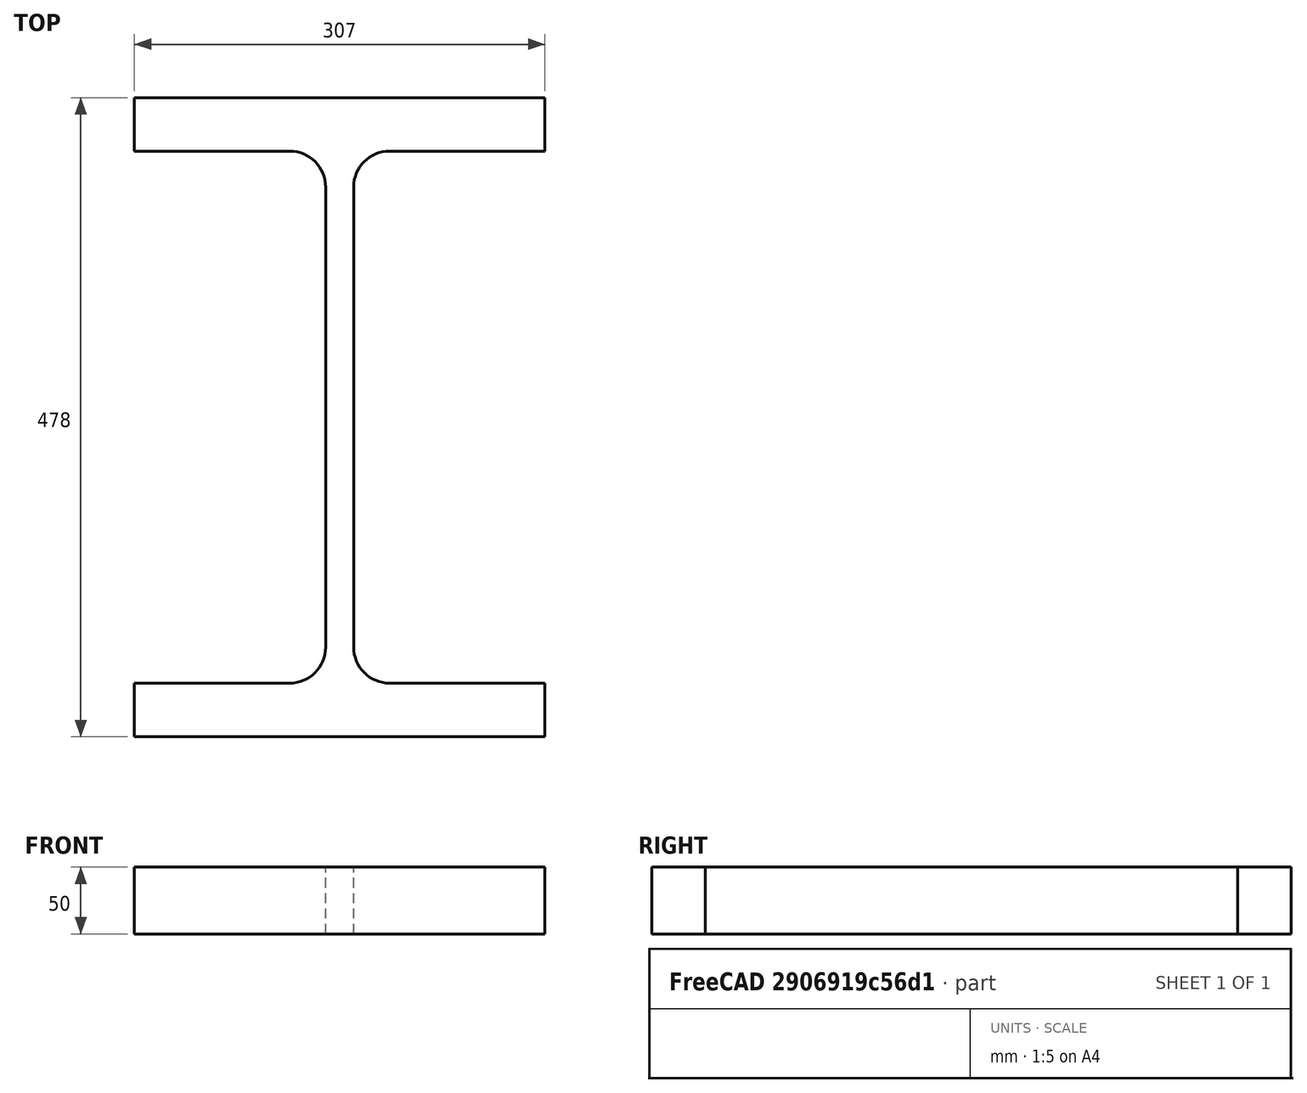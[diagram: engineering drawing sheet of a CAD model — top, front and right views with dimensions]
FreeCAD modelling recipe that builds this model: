
FCSTD DOCUMENT  (FreeCAD 0.15R4671 (Git))
Label: HE-M-Profile 450 DIN1025-4 S235JR
License: All rights reserved
LicenseURL: http://en.wikipedia.org/wiki/All_rights_reserved
objects: Sketcher::SketchObject×1, Part::Extrusion×1
note: 2 computed .brp shape members not serialized (recipe doc carries the construction recipe); baked Part::Feature solids carry a one-line shape summary decoded from their .brp

FEATURE [Sketcher::SketchObject] Sketch
  sketch-geometry (16):
    g0: LineSegment StartX=10.5 StartY=-172 StartZ=0 EndX=10.5 EndY=172 EndZ=0
    g1: LineSegment StartX=37.5 StartY=199 StartZ=0 EndX=153.5 EndY=199 EndZ=0
    g2: LineSegment StartX=153.5 StartY=199 StartZ=0 EndX=153.5 EndY=239 EndZ=0
    g3: LineSegment StartX=153.5 StartY=239 StartZ=0 EndX=-153.5 EndY=239 EndZ=0
    g4: LineSegment StartX=-153.5 StartY=239 StartZ=0 EndX=-153.5 EndY=199 EndZ=0
    g5: LineSegment StartX=-153.5 StartY=199 StartZ=0 EndX=-37.5 EndY=199 EndZ=0
    g6: LineSegment StartX=-10.5 StartY=172 StartZ=0 EndX=-10.5 EndY=-172 EndZ=0
    g7: LineSegment StartX=-37.5 StartY=-199 StartZ=0 EndX=-153.5 EndY=-199 EndZ=0
    g8: LineSegment StartX=-153.5 StartY=-199 StartZ=0 EndX=-153.5 EndY=-239 EndZ=0
    g9: LineSegment StartX=-153.5 StartY=-239 StartZ=0 EndX=153.5 EndY=-239 EndZ=0
    g10: LineSegment StartX=153.5 StartY=-239 StartZ=0 EndX=153.5 EndY=-199 EndZ=0
    g11: LineSegment StartX=153.5 StartY=-199 StartZ=0 EndX=37.5 EndY=-199 EndZ=0
    g12: ArcOfCircle CenterX=37.5 CenterY=172 CenterZ=0 NormalX=0 NormalY=0 NormalZ=1 Radius=27 StartAngle=1.5708 EndAngle=3.14159
    g13: ArcOfCircle CenterX=37.5 CenterY=-172 CenterZ=0 NormalX=0 NormalY=0 NormalZ=1 Radius=27 StartAngle=3.14159 EndAngle=4.71239
    g14: ArcOfCircle CenterX=-37.5 CenterY=172 CenterZ=0 NormalX=0 NormalY=0 NormalZ=1 Radius=27 StartAngle=0 EndAngle=1.5708
    g15: ArcOfCircle CenterX=-37.5 CenterY=-172 CenterZ=0 NormalX=0 NormalY=0 NormalZ=1 Radius=27 StartAngle=4.71239 EndAngle=6.28319
  constraints (42):
    c: Vertical(g0)
    c: Coincident(g2,g1)
    c: Vertical(g2)
    c: Coincident(g3,g2)
    c: Coincident(g4,g3)
    c: Vertical(g4)
    c: Coincident(g5,g4)
    c: Horizontal(g5)
    c: Vertical(g6)
    c: Horizontal(g7)
    c: Coincident(g8,g7)
    c: Vertical(g8)
    c: Coincident(g9,g8)
    c: Horizontal(g9)
    c: Coincident(g10,g9)
    c: Vertical(g10)
    c: Coincident(g11,g10)
    c: Horizontal(g11)
    c: Tangent(g1,g12) = 1.5708
    c: Tangent(g0,g12) = 1.5708
    c: Tangent(g0,g13) = 1.5708
    c: Tangent(g11,g13) = 1.5708
    c: Tangent(g5,g14) = 1.5708
    c: Tangent(g6,g14) = 1.5708
    c: Tangent(g6,g15) = 1.5708
    c: Tangent(g7,g15) = 1.5708
    c: Equal(g3,g9)
    c: Equal(g2,g4)
    c: Equal(g4,g8)
    c: Equal(g8,g10)
    c: Equal(g12,g14)
    c: Equal(g14,g15)
    c: Equal(g15,g13)
    c: Symmetric(g2,g3,g-2)
    c: Symmetric(g9,g8,g-2)
    c: Symmetric(g0,g6,g-2)
    c: Symmetric(g2,g9,g-1)
    c: DistanceY(g2,g9) = -478
    c: DistanceX(g3) = -307
    c: DistanceX(g0,g6) = -21
    c: DistanceY(g2) = 40
    c: Radius(g12) = 27
FEATURE [Part::Extrusion] Extrude  label="HE-M-Profile 450 DIN1025-4 S235JR"
  Base = -> Sketch
  Dir = (0,0,50)
  Solid = true
